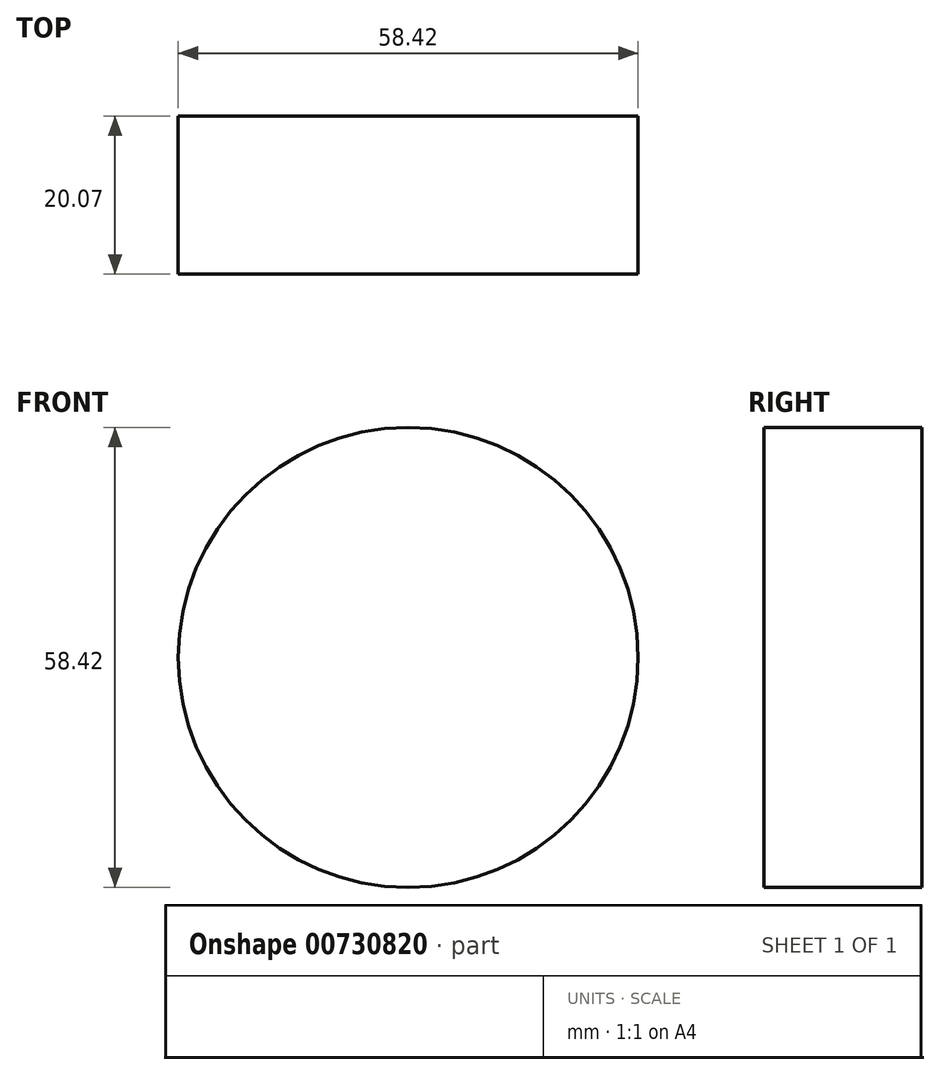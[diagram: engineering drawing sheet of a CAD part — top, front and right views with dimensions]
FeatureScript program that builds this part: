
annotation { "Feature Type Name" : "Feature", "Feature Type Description" : "" }
export const myFeature = defineFeature(function(context is Context, id is Id, definition is map)
    precondition{}
    {
        {
            var Q0;
            Q0=qCreatedBy(makeId("Front.planeOp"),FACE);
            var sketch = newSketch(context, id + "F0", { "sketchPlane" : qUnion([Q0])});
            skCircle(sketch, "E0", {"center": v(0, 0) * mm, "radius": 29.21 * mm});
            skSolve(sketch);
        }
        {
            var Q0;
            Q0 = qSketchRegion(id + "F0", true);
            extrude(context, id + "F1", {"entities" : qUnion([Q0]), "depth" : 20.07 * mm, "offsetDistance" : 25.4 * mm});
        }
    });
